# Revit family: ElectricalEquipment_Hager_TPNLighting&Power_250ADualMeterIncomerKits
name_source: partatom
category: Electrical Equipment
revit_build: Autodesk Revit 2015 (Build: 20160512_1515(x64)
units: mm (PartAtom-declared; Revit-internal decimal feet)

## types (1)
- JKD250PM
    Assembly Code = D5010
    AssetType = Fixed
    BIMObjectName = Hager_ElectricalEquipment_TripleMeteredBoards_JKD250PM
    Category = ElectricalEquipment
    ClassificationName = Uniclass2015
    ClassificationValue = Pr_80_77_28_16
    Colour = RAL 9010 White Gloss
    Default Elevation = 500 mm  [stored 1.64042 ft]
    Description = 250ADualMultiFunctionMeteredIncomer.PulsedAndModbus.SideBySide
    DocumentationLiterature = http://www.hager.co.uk
    DocumentationTechnical = http://www.hager.co.uk
    DurationUnit = Years
    EAN = 3250610459577
    ExpectedLife = 10
    Features = 250ADualMultiFunctionMeteredIncomer.PulsedAndModbus.SideBySide
    IfcExportAs = ElectricalEquipment
    Incoming = 125A
    Keynote = V
    Mains Type = AC
    Manufacturer = Hager
    ManufacturerName = Hager
    Material = MildSteel,ABS,AcousticComposite
    Model = JK250PM
    NBSDescription = ElectricalEquipment
    NBSObjectName = Hager_TripleMeteredBoards_JKD250PM
    NBSReference = Pr_80_77_28_16
    Neutral Rating = 100.00%
    NominalDepth = 166 mm
    NominalHeight = 625 mm  [stored 2.05052 ft]
    NominalLength = 0 mm  [stored 0 ft]
    NominalWidth = 930 mm  [stored 3.05118 ft]
    Outgoing = 63A
    ReplacementCost = 0
    ServiceLifeDuration = 0
    Shape = Rectangular
    Type Comments = JK250PM
    TypeName = ElectricalEquipment
    URL = http://www.hager.co.uk
    Voltage = 230V
    WarrantyDescription = See Manufacturer
    WarrantyDurationLabor = 0
    WarrantyDurationParts = 2
    WarrantyDurationUnit = Years
    WarrantyGuarantorParts = 2
    _BimSpecGuid = 0
    _BimstoreBibleVersion = V14
    _CurrentRevision = 0
    _DistributedBy = www.bimstore.co.uk

note: [stored X ft] marks values corroborated as IEEE doubles in the binary element streams (Revit-internal decimal feet)

## geometry (parser evidence)
native form markers: Blend x2, Sweep x3
no freeform markers — native parametric forms only
